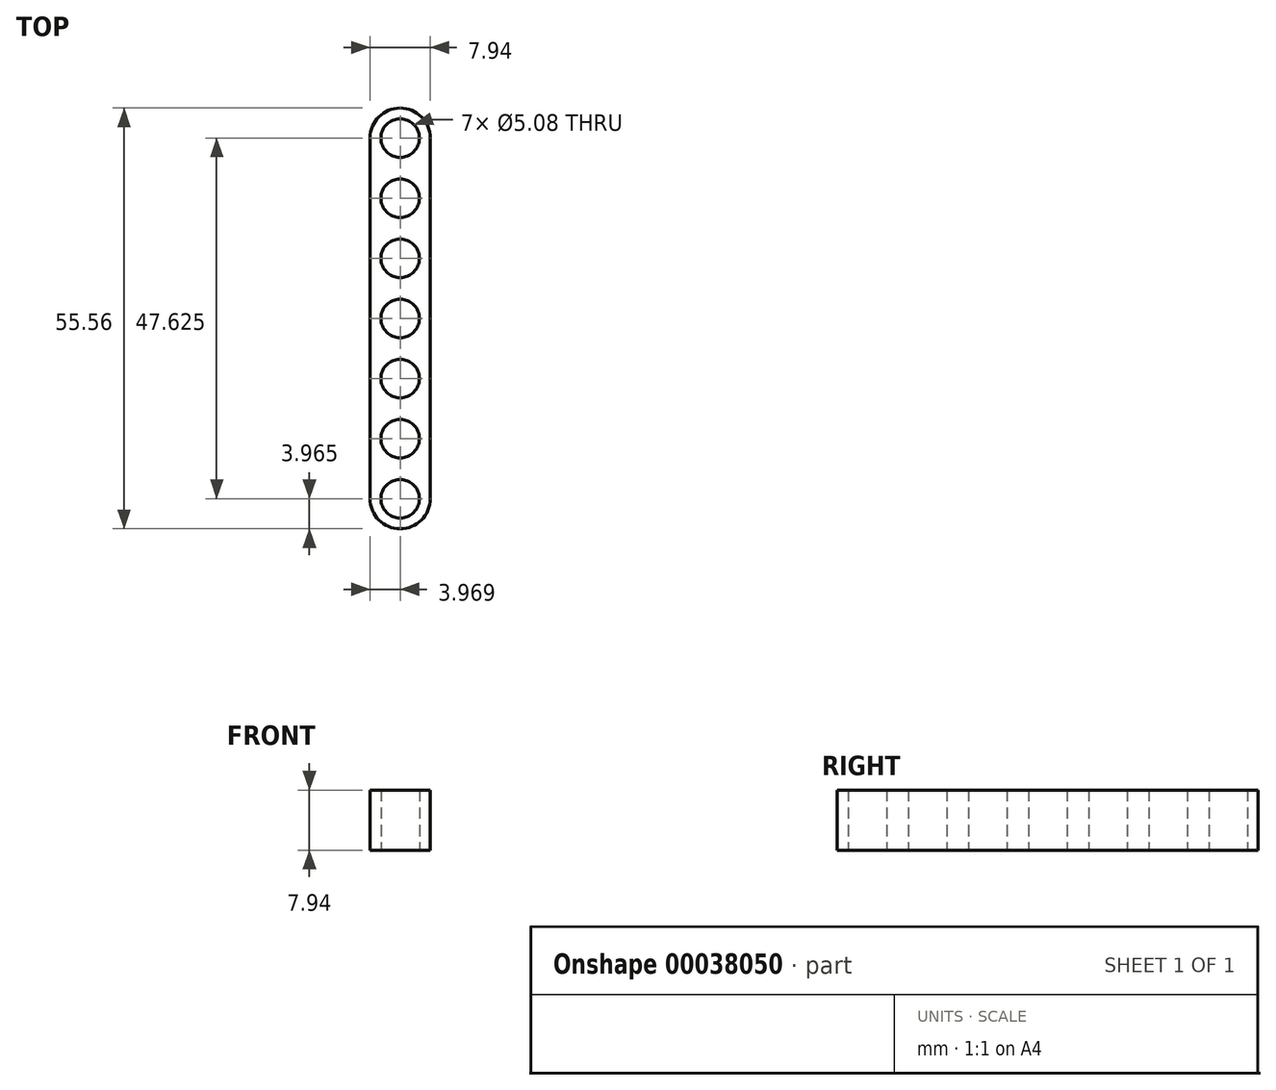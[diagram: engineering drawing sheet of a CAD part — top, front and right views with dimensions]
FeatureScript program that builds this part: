
annotation { "Feature Type Name" : "Feature", "Feature Type Description" : "" }
export const myFeature = defineFeature(function(context is Context, id is Id, definition is map)
    precondition{}
    {
        {
            var Q0;
            Q0=qCreatedBy(makeId("Top.planeOp"),FACE);
            var sketch = newSketch(context, id + "F0", { "sketchPlane" : qUnion([Q0])});
            skLineSegment(sketch, "E0.bottom", {"start": v(0, 0) * mm, "end": v(7.94, 0) * mm, "construction": true});
            skLineSegment(sketch, "E0.top", {"start": v(0, -47.62) * mm, "end": v(7.94, -47.62) * mm, "construction": true});
            skLineSegment(sketch, "E0.left", {"start": v(0, 0) * mm, "end": v(0, -47.62) * mm});
            skLineSegment(sketch, "E0.right", {"start": v(7.94, 0) * mm, "end": v(7.94, -47.62) * mm});
            skLineSegment(sketch, "E1", {"start": v(3.97, -23.81) * mm, "end": v(3.97, -31.75) * mm, "construction": true});
            skLineSegment(sketch, "E2", {"start": v(3.97, -31.75) * mm, "end": v(3.97, -39.69) * mm, "construction": true});
            skLineSegment(sketch, "E3", {"start": v(3.97, -39.69) * mm, "end": v(3.97, -47.62) * mm, "construction": true});
            skArc(sketch, "E4", {"start": v(7.94, 0) * mm, "mid": v(3.97, 3.97) * mm, "end": v(0, 0) * mm});
            skArc(sketch, "E5", {"start": v(0, -47.62) * mm, "mid": v(3.97, -51.6) * mm, "end": v(7.94, -47.62) * mm});
            skCircle(sketch, "E6", {"center": v(3.97, 0) * mm, "radius": 2.54 * mm});
            skCircle(sketch, "E7", {"center": v(3.97, -23.81) * mm, "radius": 2.54 * mm});
            skCircle(sketch, "E8", {"center": v(3.97, -31.75) * mm, "radius": 2.54 * mm});
            skCircle(sketch, "E9", {"center": v(3.97, -39.69) * mm, "radius": 2.54 * mm});
            skCircle(sketch, "E10", {"center": v(3.97, -47.62) * mm, "radius": 2.54 * mm});
            skLineSegment(sketch, "E11", {"start": v(3.97, -23.81) * mm, "end": v(3.97, -15.87) * mm, "construction": true});
            skLineSegment(sketch, "E12", {"start": v(3.97, -15.87) * mm, "end": v(3.97, -7.94) * mm, "construction": true});
            skLineSegment(sketch, "E13", {"start": v(3.97, -7.94) * mm, "end": v(3.97, 0) * mm, "construction": true});
            skCircle(sketch, "E14", {"center": v(3.97, -15.87) * mm, "radius": 2.54 * mm});
            skCircle(sketch, "E15", {"center": v(3.97, -7.94) * mm, "radius": 2.54 * mm});
            skSolve(sketch);
        }
        {
            var Q0;
            Q0=qSketchRegion(id+"F0",true);
            extrude(context, id + "F1", {"entities" : qUnion([Q0]), "depth" : 7.94 * mm});
        }
    });
